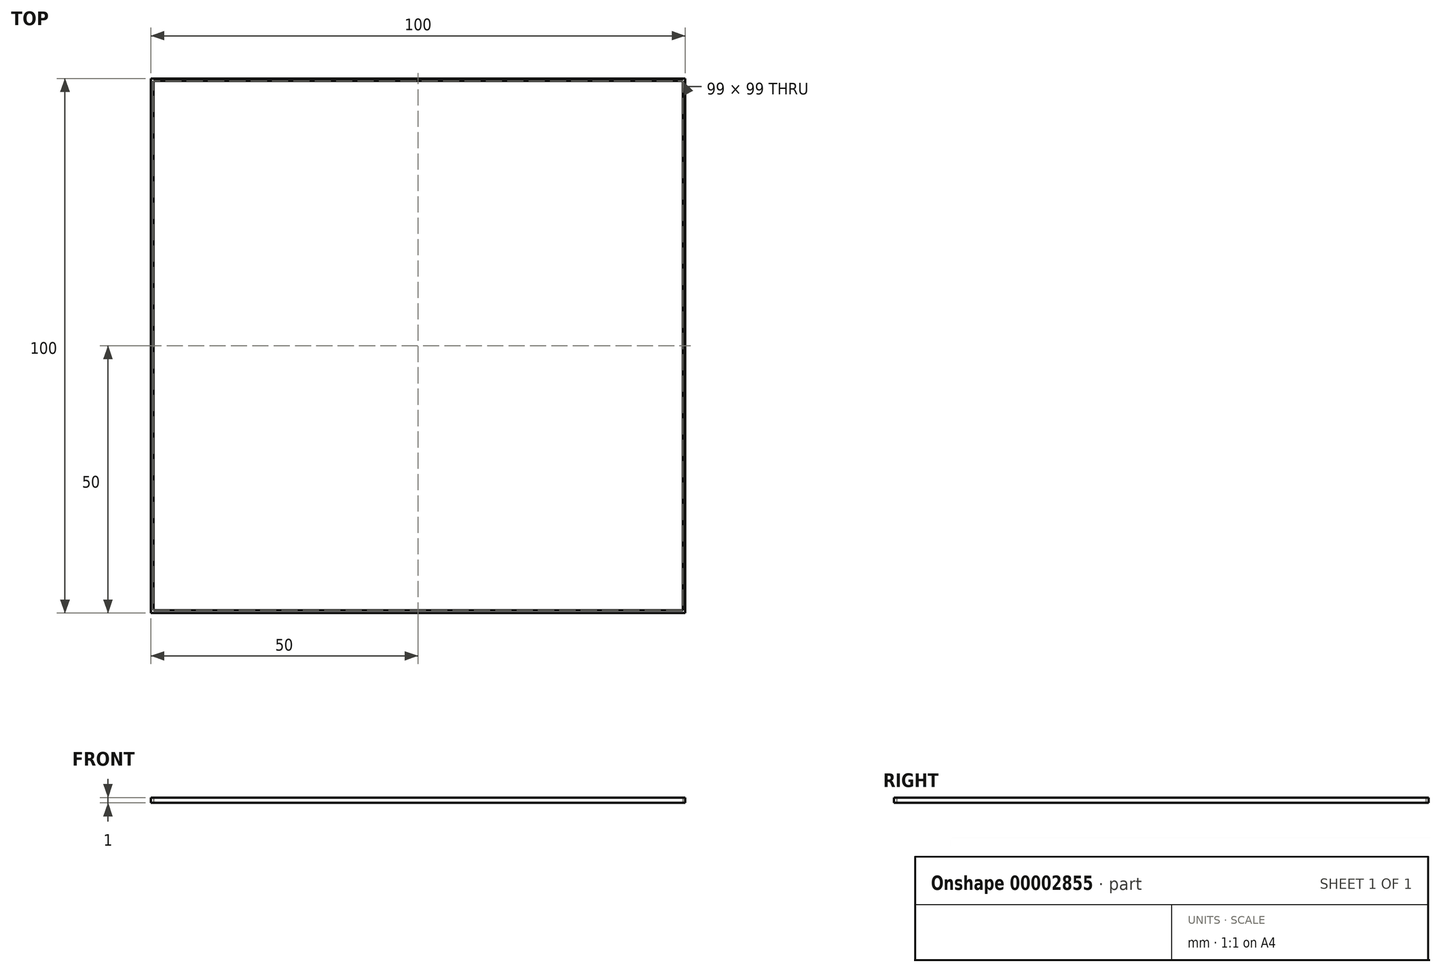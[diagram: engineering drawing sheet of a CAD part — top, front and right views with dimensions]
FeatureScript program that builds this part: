
annotation { "Feature Type Name" : "Feature", "Feature Type Description" : "" }
export const myFeature = defineFeature(function(context is Context, id is Id, definition is map)
    precondition{}
    {
        {
            var Q0;
            Q0=qCreatedBy(makeId("Top.planeOp"),FACE);
            var sketch = newSketch(context, id + "F0", { "sketchPlane" : qUnion([Q0])});
            skLineSegment(sketch, "E0.bottom", {"start": v(-57.02, 31.37) * mm, "end": v(42.98, 31.37) * mm});
            skLineSegment(sketch, "E0.top", {"start": v(-57.02, -68.63) * mm, "end": v(42.98, -68.63) * mm});
            skLineSegment(sketch, "E0.left", {"start": v(-57.02, 31.37) * mm, "end": v(-57.02, -68.63) * mm});
            skLineSegment(sketch, "E0.right", {"start": v(42.98, 31.37) * mm, "end": v(42.98, -68.63) * mm});
            skLineSegment(sketch, "E1.bottom", {"start": v(-56.52, 30.87) * mm, "end": v(42.48, 30.87) * mm});
            skLineSegment(sketch, "E1.top", {"start": v(-56.52, -68.13) * mm, "end": v(42.48, -68.13) * mm});
            skLineSegment(sketch, "E1.left", {"start": v(-56.52, 30.87) * mm, "end": v(-56.52, -68.13) * mm});
            skLineSegment(sketch, "E1.right", {"start": v(42.48, 30.87) * mm, "end": v(42.48, -68.13) * mm});
            skSolve(sketch);
        }
        {
            var Q0;
            Q0=makeQuery(id+"F0.imprint","IMPRINT",FACE,{"disambiguationData":[TD([[makeQuery(id+"F0.imprint","IMPRINT",EDGE,{"derivedFrom":sQuery(id+"F0.wireOp",EDGE,"E0.bottom")}),-1.0]])]});
            extrude(context, id + "F1", {"entities" : qUnion([Q0]), "depth" : 1 * mm});
        }
    });
